# Revit family: streetlight_sl_11_iq_midi___pc-l_5xc3e11g08me_d623
name_source: partatom
category: Lighting Fixtures
units: mm (PartAtom-declared; Revit-internal decimal feet)

## family parameters
Cut with Voids When Loaded = No
Host = Face
Light Source = No
Part Type = Normal
Room Calculation Point = No
Round Connector Dimension = Use Diameter
Shared = No

## types (1)
- --- (1 x LED, 9590 lm, 124.5 W, 1800K)
    Apparent Load = 125 VA
    CIE Flux Codes = 37 73 96 100 100
    Color Rendering = 70
    Color Temperature = 1800K
    Default Elevation = 1800 mm  [stored 5.90551 ft]
    Description = Streetlight SL 11 iQ midi, mast luminaire, primary light control with 3 zone facetted reflector, of plastic, silver coated, highly specular, primary optical cover: cover, of PMMA, transparent, light distribution: PC-L, light emission: direct distribution, primary light characteristic: asymmetric, left, installation type: post-top, side-entry, lamps: LED, High Power LED, rated values: 9.590lm | 124,5W | 77lm/W (begin service life); end service life: 9.590lm | 131,6W; at 50% lumin. flux: 4.795lm | 55,1W | 87lm/W, colour temperature: 1800K, colour rendering: CRI > 70, light colour: 718, light setting 1 begin service life: 100% | 9.590lm | 124,5W | 77lm/W | 1.800K, light setting 1 end service life: 131,6W, further light settings possible, control: Street-Remote, Auto-Match, Temp-Guard, Lumen-Switch, Night-Set, Smart-Wire, Light-Fading, Desk-Remote (wireless, voltage-free reading and setting of iQ features in the workshop via application-optimized NFC function/RFID function), optimised constant luminous flux control (CLO 2.0), pre-setting: linear dimming characteristic, with cable H07RN-F 5x 1.5mm², mains connection: 230..240V, AC, 50/60Hz, connection cable pre-assembled, cable length: 12,5m, luminaire housing, of diecast aluminium, powder-coated, SITECO metallic grey (DB 702S), please order mast flange separately, inclination adjustable without tools: 0°, 5°, 10°, 15° (post-top) | 0°, -5°, -10°, -15° (side-entry), sealing non-destructively replaceable, multi-level sealing system, length: 780mm, width: 376mm, height: 118mm, mast flange for spigot size: 42mm (side-entry): 5XC10008XM4, 60/48mm (side-entry/post-top): 5XC10108XM2, 76/60mm (side-entry/post-top): 5XC10108XM1, equipment: Power, protection rating (complete): IP66, insulation class (complete): insulation class II (safety insulation), certification: CE, ENEC, ENEC+, VDE, impact resistance: IK10, permissible operating ambient temperature for outdoor applications: -25..+50°C, standard-compliant lighting for roads and squares, Environmental Product Declaration (EPD) tested and certified by an independent institute, packaging unit: 1 piece

Light Distribution: PC-L
    Height = 118 mm
    Lamp = 1 x LED
    Lamp Light Flux = 9590 lm
    Lamp Power = 124.5 W
    Lamp count = 1
    Length = 780 mm
    Luminous efficacy = 77 lm/W
    Manufacturer = Siteco
    ModVariant = No
    Model = 5XC3E11G08ME
    Number of Poles = 1
    OnlyDefault = Yes
    Power Factor = 1
    Product Name = Streetlight SL 11 iQ midi | PC-L
    Product group = mast luminaire | pylon top
    ProductGroupID = 6100
    Protection Class = Protection class II
    Protection Degree = IP 66
    RLX_Detail_Level = 1
    RLX_Emergency_Light_Flux = 0 lm
    RLX_Emergency_Type = 0
    RLX_Emergency_Type_DB = No
    RlxData = <blob elided: 74957 chars, md5=1ee9e997>
    Socket = socket
    Standby Power = 0 W
    System Light Flux = 9590 lm
    System Power = 125 W
    Type Comments = factory setting: luminous flux: 100 % | dim-lin: 254 | 554 mA
    Type Image = l_1005960.jpg
    URL = http://relux.com
    VarID = @adj_085769
    Voltage = 0 V
    Weight = 0.00 kg
    Width = 376 mm

note: [stored X ft] marks values corroborated as IEEE doubles in the binary element streams (Revit-internal decimal feet)

## geometry (parser evidence)
native form markers: Sweep x9
no freeform markers — native parametric forms only
